# Revit family: 63_PHILIPS_RC342B FLexBlend Recessed W31L125 PCV
name_source: partatom
category: Lighting Fixtures
revit_build: Autodesk Revit 2016 (Build: 20161004_0715(x64)
units: mm (PartAtom-declared; Revit-internal decimal feet)

## family parameters
Cut with Voids When Loaded = No
Host = Face
Light Source = No
Part Type = Normal
Room Calculation Point = No
Round Connector Dimension = Use Diameter
Shared = No

## types (1)
- 63_PHILIPS_RC342B FLexBlend Recessed W31L125 PCV
    Apparent Load = 18 VA
    BIM Library - URL = http://www.lighting.philips.com
    Ceiling thickness = 13 mm  [stored 0.0426509 ft]
    Content modified date = 25-09-2018
    Content version = 1.0
    Cut out length = 1237 mm  [stored 4.0584 ft]
    Cut out width = 300 mm
    Default Elevation = 0 mm  [stored 0 ft]
    Description = FlexBlend
    Distance to Rim hor = 37 mm
    Distance to Rim ver = 80 mm  [stored 0.262467 ft]
    EOC/12nc = 12NC CODE
    ETIM code = EC002892
    ETIM code URL = https://prod.etim-international.com
    Fixture code = FIXTURE CODE
    Height = 61 mm  [stored 0.200131 ft]
    Height_01 = 77 mm  [stored 0.252625 ft]
    Housing Length = 1173 mm  [stored 3.84843 ft]
    Housing Width = 171 mm  [stored 0.561024 ft]
    Image = <None>
    Installation space height = 150 mm  [stored 0.492126 ft]
    Lamp = LAMP NAME
    Lamp type = RC342B IES Data : POE W31L125 1 xLED28S_830 MLO
    Last IES update = 12-03-2019
    Length = 1247 mm  [stored 4.09121 ft]
    Light Plane to Rim hor = 12 mm  [stored 0.0393701 ft]
    Light Plane to Rim ver = 90 mm  [stored 0.295276 ft]
    Light source = 2 mm  [stored 0.00656168 ft]
    Manufacturer = Philips
    Model = RC342B W31L125 PCV
    Order code = ORDER CODE
    Product catalog - URL = WEBPAGE MODEL
    Rim height = 6 mm  [stored 0.019685 ft]
    Rotation XY = 0.00°
    Rotation XZ = 0.00°
    Type Comments = Recessed
    URL = http://www.lighting.philips.com
    Voltage (V) = 230 V
    Width = 310 mm

note: [stored X ft] marks values corroborated as IEEE doubles in the binary element streams (Revit-internal decimal feet)

## geometry (parser evidence)
native form markers: Blend x12, Sweep x18
no freeform markers — native parametric forms only
